AUTODESK INVENTOR PART (.ipt)
format: ipt  version: 2017 (Build 210142000, 142)  size: 113,664 bytes
history: native  units: mm
features: other x4, extrude x1, sketch x1, reference x1
ambient origin geometry x8: Origin, YZ Plane, XZ Plane, XY Plane, X Axis, Y Axis, Z Axis, Center Point
feature tree (7):
  other  "Sólido1"
  extrude  "Extrusión1"  Depth=4.0mm
  sketch  "Boceto1"  dims[d0=70.0mm d1=4.0mm d2=65.0mm d3=2.0mm d4=11.0mm d5=28.0mm d6=25.7mm d7=16.0mm d8=4.0mm d9=4.0mm d10=0.0mm]
  reference  "Referencia1"
  other  "<userpath>\Documents\GitHub\actor-re-actor\models\inventor-caja\Case\Case-D.iam"
  other  "Case-D.iam"
  other  "Tapa Enchufes b:1"
